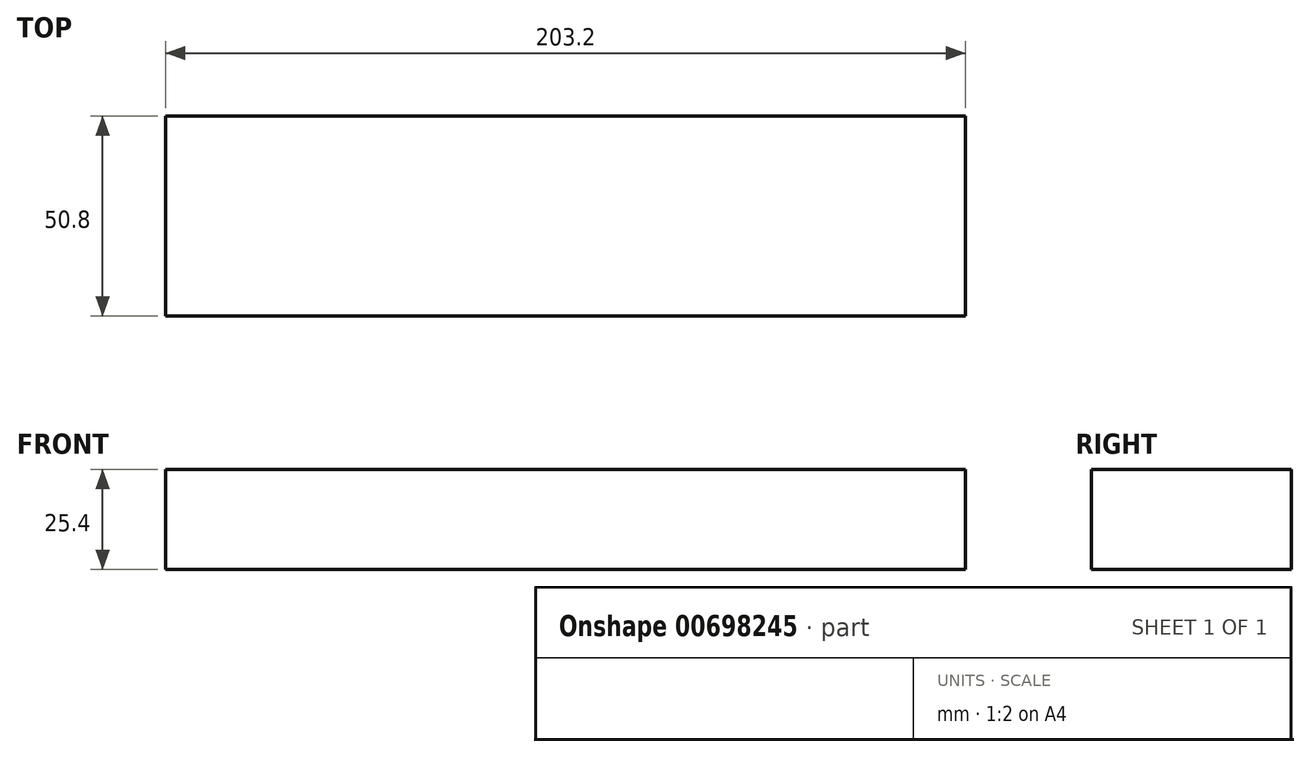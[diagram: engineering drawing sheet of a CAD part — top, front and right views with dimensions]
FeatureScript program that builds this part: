
annotation { "Feature Type Name" : "Feature", "Feature Type Description" : "" }
export const myFeature = defineFeature(function(context is Context, id is Id, definition is map)
    precondition{}
    {
        {
            var Q0;
            Q0=qCreatedBy(makeId("Top.planeOp"),FACE);
            var sketch = newSketch(context, id + "F0", { "sketchPlane" : qUnion([Q0])});
            skLineSegment(sketch, "E0.bottom", {"start": v(-100.6, 4.64) * mm, "end": v(102.6, 4.64) * mm});
            skLineSegment(sketch, "E0.top", {"start": v(-100.6, -46.16) * mm, "end": v(102.6, -46.16) * mm});
            skLineSegment(sketch, "E0.left", {"start": v(-100.6, 4.64) * mm, "end": v(-100.6, -46.16) * mm});
            skLineSegment(sketch, "E0.right", {"start": v(102.6, 4.64) * mm, "end": v(102.6, -46.16) * mm});
            skSolve(sketch);
        }
        {
            var Q0;
            Q0 = qSketchRegion(id + "F0", true);
            extrude(context, id + "F1", {"entities" : qUnion([Q0]), "depth" : 25.4 * mm, "offsetDistance" : 25.4 * mm});
        }
    });
